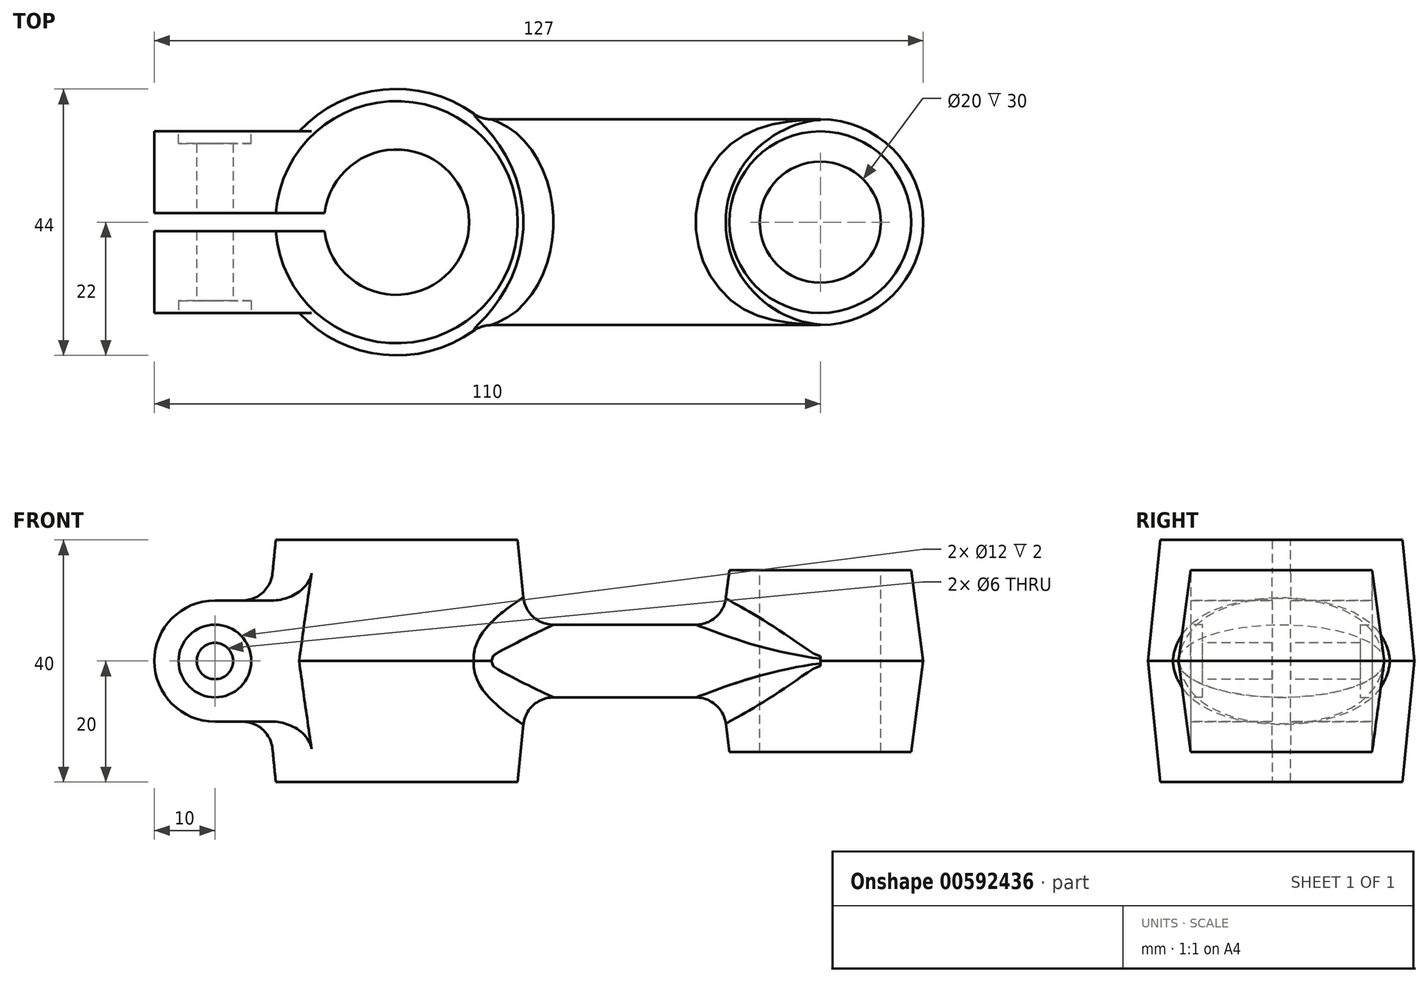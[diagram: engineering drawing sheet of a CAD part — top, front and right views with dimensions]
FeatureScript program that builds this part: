
annotation { "Feature Type Name" : "Feature", "Feature Type Description" : "" }
export const myFeature = defineFeature(function(context is Context, id is Id, definition is map)
    precondition{}
    {
        {
            var Q0;
            Q0=qCreatedBy(makeId("Right.planeOp"),FACE);
            var sketch = newSketch(context, id + "F0", { "sketchPlane" : qUnion([Q0])});
            skEllipse(sketch, "E0", {"center": v(0, 0) * mm, "majorRadius": 17 * mm, "minorRadius": 6 * mm, "majorAxis": v(-1, 0)});
            skSolve(sketch);
        }
        {
            var Q0;
            Q0=makeQuery(id+"F0.imprint","IMPRINT",FACE,{"disambiguationData":[TD([[makeQuery(id+"F0.imprint","IMPRINT",EDGE,{"derivedFrom":sQuery(id+"F0.wireOp",EDGE,"E0")}),1.0]])]});
            extrude(context, id + "F1", {"entities" : qUnion([Q0]), "endBound" : BoundingType.SYMMETRIC, "depth" : 70 * mm, "offsetDistance" : 25 * mm});
        }
        {
            var Q0;
            Q0=qCreatedBy(makeId("Front.planeOp"),FACE);
            var sketch = newSketch(context, id + "F2", { "sketchPlane" : qUnion([Q0])});
            skLineSegment(sketch, "E1", {"start": v(-35, 20) * mm, "end": v(-55, 20) * mm});
            skLineSegment(sketch, "E2", {"start": v(-55, 20) * mm, "end": v(-57, 0) * mm});
            skLineSegment(sketch, "E3", {"start": v(-57, 0) * mm, "end": v(-55, -20) * mm});
            skLineSegment(sketch, "E4", {"start": v(-55, -20) * mm, "end": v(-35, -20) * mm});
            skLineSegment(sketch, "E5", {"start": v(-35, -20) * mm, "end": v(-35, 20) * mm});
            skSolve(sketch);
        }
        {
            var Q0;
            Q0 = qSketchRegion(id + "F2", true);
            var Q1;
            Q1=sQuery(id+"F2.wireOp",EDGE,"E5");
            revolve(context, id + "F3", {"operationType" : NewBodyOperationType.ADD, "entities" : qUnion([Q0]), "axis" : qUnion([Q1]), "revolveType" : RevolveType.FULL});
        }
        {
            var Q0;
            Q0=qCreatedBy(makeId("Front.planeOp"),FACE);
            var sketch = newSketch(context, id + "F4", { "sketchPlane" : qUnion([Q0])});
            skLineSegment(sketch, "E6", {"start": v(35, 15) * mm, "end": v(50, 15) * mm});
            skLineSegment(sketch, "E7", {"start": v(50, 15) * mm, "end": v(52, 0) * mm});
            skLineSegment(sketch, "E8", {"start": v(52, 0) * mm, "end": v(50, -15) * mm});
            skLineSegment(sketch, "E9", {"start": v(50, -15) * mm, "end": v(35, -15) * mm});
            skLineSegment(sketch, "E10", {"start": v(35, -15) * mm, "end": v(35, 15) * mm});
            skSolve(sketch);
        }
        {
            var Q0;
            Q0 = qSketchRegion(id + "F4", true);
            var Q1;
            Q1=sQuery(id+"F4.wireOp",EDGE,"E10");
            revolve(context, id + "F5", {"operationType" : NewBodyOperationType.ADD, "entities" : qUnion([Q0]), "axis" : qUnion([Q1]), "revolveType" : RevolveType.FULL});
        }
        {
            var Q0;
            Q0=qCreatedBy(makeId("Front.planeOp"),FACE);
            var sketch = newSketch(context, id + "F6", { "sketchPlane" : qUnion([Q0])});
            skLineSegment(sketch, "E11.bottom", {"start": v(-65, 10) * mm, "end": v(-35, 10) * mm});
            skLineSegment(sketch, "E11.top", {"start": v(-65, -10) * mm, "end": v(-35, -10) * mm});
            skLineSegment(sketch, "E11.right", {"start": v(-35, 10) * mm, "end": v(-35, -10) * mm});
            skArc(sketch, "E12", {"start": v(-65, 10) * mm, "mid": v(-75, 0) * mm, "end": v(-65, -10) * mm});
            skSolve(sketch);
        }
        {
            var Q0;
            Q0 = qSketchRegion(id + "F6", true);
            extrude(context, id + "F7", {"entities" : qUnion([Q0]), "operationType" : NewBodyOperationType.ADD, "endBound" : BoundingType.SYMMETRIC, "depth" : 30 * mm, "offsetDistance" : 25 * mm});
        }
        {
            var Q0;
            Q0=makeQuery(id+"F3.opRevolve","SWEPT_FACE",FACE,{"disambiguationData":[OSD([sQuery(id+"F2.wireOp",EDGE,"E1")])]});
            var sketch = newSketch(context, id + "F8", { "sketchPlane" : qUnion([Q0])});
            skArc(sketch, "E13", {"start": v(-46.9, -1.5) * mm, "mid": v(-23, 0) * mm, "end": v(-46.9, 1.5) * mm});
            skCircle(sketch, "E14", {"center": v(35, 0) * mm, "radius": 10 * mm});
            skLineSegment(sketch, "E15", {"start": v(-46.9, 1.5) * mm, "end": v(-75, 1.5) * mm});
            skLineSegment(sketch, "E16", {"start": v(-75, 1.5) * mm, "end": v(-75, -1.5) * mm});
            skLineSegment(sketch, "E17", {"start": v(-75, -1.5) * mm, "end": v(-46.9, -1.5) * mm});
            skPoint(sketch, "E18.orphan", {"position": v(-35, -1.5) * mm});
            skPoint(sketch, "E19.orphan", {"position": v(-35, 1.5) * mm});
            skSolve(sketch);
        }
        {
            var Q0;
            Q0 = qSketchRegion(id + "F8", true);
            extrude(context, id + "F9", {"entities" : qUnion([Q0]), "operationType" : NewBodyOperationType.REMOVE, "endBound" : BoundingType.THROUGH_ALL, "oppositeDirection" : true, "depth" : 25 * mm, "offsetDistance" : 25 * mm});
        }
        {
            var Q0;
            Q0=makeQuery(id+"F3.boolean.opBoolean","INTERSECT",EDGE,{"derivedFrom":[makeQuery(id+"F1.opExtrude","SWEPT_FACE",FACE,{"disambiguationData":[OSD([sQuery(id+"F0.wireOp",EDGE,"E0")])]}),makeQuery(id+"F3.opRevolve","SWEPT_FACE",FACE,{"disambiguationData":[OSD([sQuery(id+"F2.wireOp",EDGE,"E2")])]})]});
            var Q1;
            Q1=makeQuery(id+"F5.boolean.opBoolean","INTERSECT",EDGE,{"derivedFrom":[makeQuery(id+"F1.opExtrude","SWEPT_FACE",FACE,{"disambiguationData":[OSD([sQuery(id+"F0.wireOp",EDGE,"E0")])]}),makeQuery(id+"F5.opRevolve","SWEPT_FACE",FACE,{"disambiguationData":[OSD([sQuery(id+"F4.wireOp",EDGE,"E7")])]})]});
            var Q2;
            Q2=makeQuery(id+"F5.boolean.opBoolean","INTERSECT",EDGE,{"derivedFrom":[makeQuery(id+"F1.opExtrude","SWEPT_FACE",FACE,{"disambiguationData":[OSD([sQuery(id+"F0.wireOp",EDGE,"E0")])]}),makeQuery(id+"F5.opRevolve","SWEPT_FACE",FACE,{"disambiguationData":[OSD([sQuery(id+"F4.wireOp",EDGE,"E8")])]})]});
            var Q3;
            Q3=makeQuery(id+"F3.boolean.opBoolean","INTERSECT",EDGE,{"derivedFrom":[makeQuery(id+"F1.opExtrude","SWEPT_FACE",FACE,{"disambiguationData":[OSD([sQuery(id+"F0.wireOp",EDGE,"E0")])]}),makeQuery(id+"F3.opRevolve","SWEPT_FACE",FACE,{"disambiguationData":[OSD([sQuery(id+"F2.wireOp",EDGE,"E3")])]})]});
            var Q4;
            {var subQ0=makeQuery(id+"F3.opRevolve","SWEPT_FACE",FACE,{"disambiguationData":[OSD([sQuery(id+"F2.wireOp",EDGE,"E2")])]});var subQ1=sQuery(id+"F6.wireOp",EDGE,"E11.bottom");var subQ2=makeQuery(id+"F7.opExtrude","SWEPT_FACE",FACE,{"disambiguationData":[OSD([subQ1])]});Q4=makeQuery(id+"F9.boolean.opBoolean","SPLIT",EDGE,{"disambiguationData":[TD([makeQuery(id+"F9.opExtrude","SWEPT_FACE",FACE,{"disambiguationData":[OSD([sQuery(id+"F8.wireOp",EDGE,"E17")])]})])],"derivedFrom":makeQuery(id+"F7.boolean.opBoolean","INTERSECT",EDGE,{"derivedFrom":[subQ0,subQ2]})});}
            var Q5;
            {var subQ0=makeQuery(id+"F3.opRevolve","SWEPT_FACE",FACE,{"disambiguationData":[OSD([sQuery(id+"F2.wireOp",EDGE,"E2")])]});var subQ1=sQuery(id+"F6.wireOp",EDGE,"E11.bottom");var subQ2=makeQuery(id+"F7.opExtrude","SWEPT_FACE",FACE,{"disambiguationData":[OSD([subQ1])]});Q5=makeQuery(id+"F9.boolean.opBoolean","SPLIT",EDGE,{"disambiguationData":[TD([makeQuery(id+"F9.opExtrude","SWEPT_FACE",FACE,{"disambiguationData":[OSD([sQuery(id+"F8.wireOp",EDGE,"E15")])]})])],"derivedFrom":makeQuery(id+"F7.boolean.opBoolean","INTERSECT",EDGE,{"derivedFrom":[subQ0,subQ2]})});}
            var Q6;
            {var subQ0=makeQuery(id+"F3.opRevolve","SWEPT_FACE",FACE,{"disambiguationData":[OSD([sQuery(id+"F2.wireOp",EDGE,"E3")])]});var subQ1=sQuery(id+"F6.wireOp",EDGE,"E11.top");var subQ2=makeQuery(id+"F7.opExtrude","SWEPT_FACE",FACE,{"disambiguationData":[OSD([subQ1])]});Q6=makeQuery(id+"F9.boolean.opBoolean","SPLIT",EDGE,{"disambiguationData":[TD([makeQuery(id+"F9.opExtrude","SWEPT_FACE",FACE,{"disambiguationData":[OSD([sQuery(id+"F8.wireOp",EDGE,"E17")])]})])],"derivedFrom":makeQuery(id+"F7.boolean.opBoolean","INTERSECT",EDGE,{"derivedFrom":[subQ0,subQ2]})});}
            var Q7;
            {var subQ0=makeQuery(id+"F3.opRevolve","SWEPT_FACE",FACE,{"disambiguationData":[OSD([sQuery(id+"F2.wireOp",EDGE,"E3")])]});var subQ1=sQuery(id+"F6.wireOp",EDGE,"E11.top");var subQ2=makeQuery(id+"F7.opExtrude","SWEPT_FACE",FACE,{"disambiguationData":[OSD([subQ1])]});Q7=makeQuery(id+"F9.boolean.opBoolean","SPLIT",EDGE,{"disambiguationData":[TD([makeQuery(id+"F9.opExtrude","SWEPT_FACE",FACE,{"disambiguationData":[OSD([sQuery(id+"F8.wireOp",EDGE,"E15")])]})])],"derivedFrom":makeQuery(id+"F7.boolean.opBoolean","INTERSECT",EDGE,{"derivedFrom":[subQ0,subQ2]})});}
            fillet(context, id + "F10", {"entities" : qUnion([Q0, Q1, Q2, Q3, Q4, Q5, Q6, Q7]), "radius" : 5 * mm, "tangentPropagation" : true, "allowEdgeOverflow" : false});
        }
        {
            var Q0;
            Q0=makeQuery(id+"F7.opExtrude","CAP_FACE",FACE,{"disambiguationData":[OSD([sQuery(id+"F6.wireOp",EDGE,"E11.bottom"),sQuery(id+"F6.wireOp",EDGE,"E11.top"),sQuery(id+"F6.wireOp",EDGE,"E11.right"),sQuery(id+"F6.wireOp",EDGE,"E12")])],"isStart":false});
            var sketch = newSketch(context, id + "F11", { "sketchPlane" : qUnion([Q0])});
            skCircle(sketch, "E20", {"center": v(-65, 0) * mm, "radius": 6 * mm});
            skSolve(sketch);
        }
        {
            var Q0;
            Q0=makeQuery(id+"F11.imprint","IMPRINT",FACE,{"disambiguationData":[TD([[makeQuery(id+"F11.imprint","IMPRINT",EDGE,{"derivedFrom":sQuery(id+"F11.wireOp",EDGE,"E20")}),1.0]])]});
            var Q1;
            Q1=sQuery(id+"F11.wireOp",EDGE,"E20");
            extrude(context, id + "F12", {"entities" : qUnion([Q0]), "operationType" : NewBodyOperationType.REMOVE, "surfaceEntities" : qUnion([Q1]), "oppositeDirection" : true, "depth" : 2 * mm, "offsetDistance" : 25 * mm});
        }
        {
            var Q0;
            Q0=makeQuery(id+"F7.opExtrude","CAP_FACE",FACE,{"disambiguationData":[OSD([sQuery(id+"F6.wireOp",EDGE,"E11.bottom"),sQuery(id+"F6.wireOp",EDGE,"E11.top"),sQuery(id+"F6.wireOp",EDGE,"E11.right"),sQuery(id+"F6.wireOp",EDGE,"E12")])],"isStart":true});
            var sketch = newSketch(context, id + "F13", { "sketchPlane" : qUnion([Q0])});
            skCircle(sketch, "E21", {"center": v(65, 0) * mm, "radius": 6 * mm});
            skSolve(sketch);
        }
        {
            var Q0;
            Q0=makeQuery(id+"F13.imprint","IMPRINT",FACE,{"disambiguationData":[TD([[makeQuery(id+"F13.imprint","IMPRINT",EDGE,{"derivedFrom":sQuery(id+"F13.wireOp",EDGE,"E21")}),1.0]])]});
            extrude(context, id + "F14", {"entities" : qUnion([Q0]), "operationType" : NewBodyOperationType.REMOVE, "oppositeDirection" : true, "depth" : 2 * mm, "offsetDistance" : 25 * mm});
        }
        {
            var Q0;
            Q0=makeQuery(id+"F12.boolean.opBoolean","COPY",FACE,{"derivedFrom":makeQuery(id+"F12.opExtrude","CAP_FACE",FACE,{"disambiguationData":[OSD([sQuery(id+"F11.wireOp",EDGE,"E20")])],"isStart":false})});
            var sketch = newSketch(context, id + "F15", { "sketchPlane" : qUnion([Q0])});
            skCircle(sketch, "E22", {"center": v(-65, 0) * mm, "radius": 3 * mm});
            skSolve(sketch);
        }
        {
            var Q0;
            Q0=makeQuery(id+"F15.imprint","IMPRINT",FACE,{"disambiguationData":[TD([[makeQuery(id+"F15.imprint","IMPRINT",EDGE,{"derivedFrom":sQuery(id+"F15.wireOp",EDGE,"E22")}),1.0]])]});
            extrude(context, id + "F16", {"entities" : qUnion([Q0]), "operationType" : NewBodyOperationType.REMOVE, "endBound" : BoundingType.THROUGH_ALL, "oppositeDirection" : true, "depth" : 25 * mm, "offsetDistance" : 25 * mm});
        }
    });
